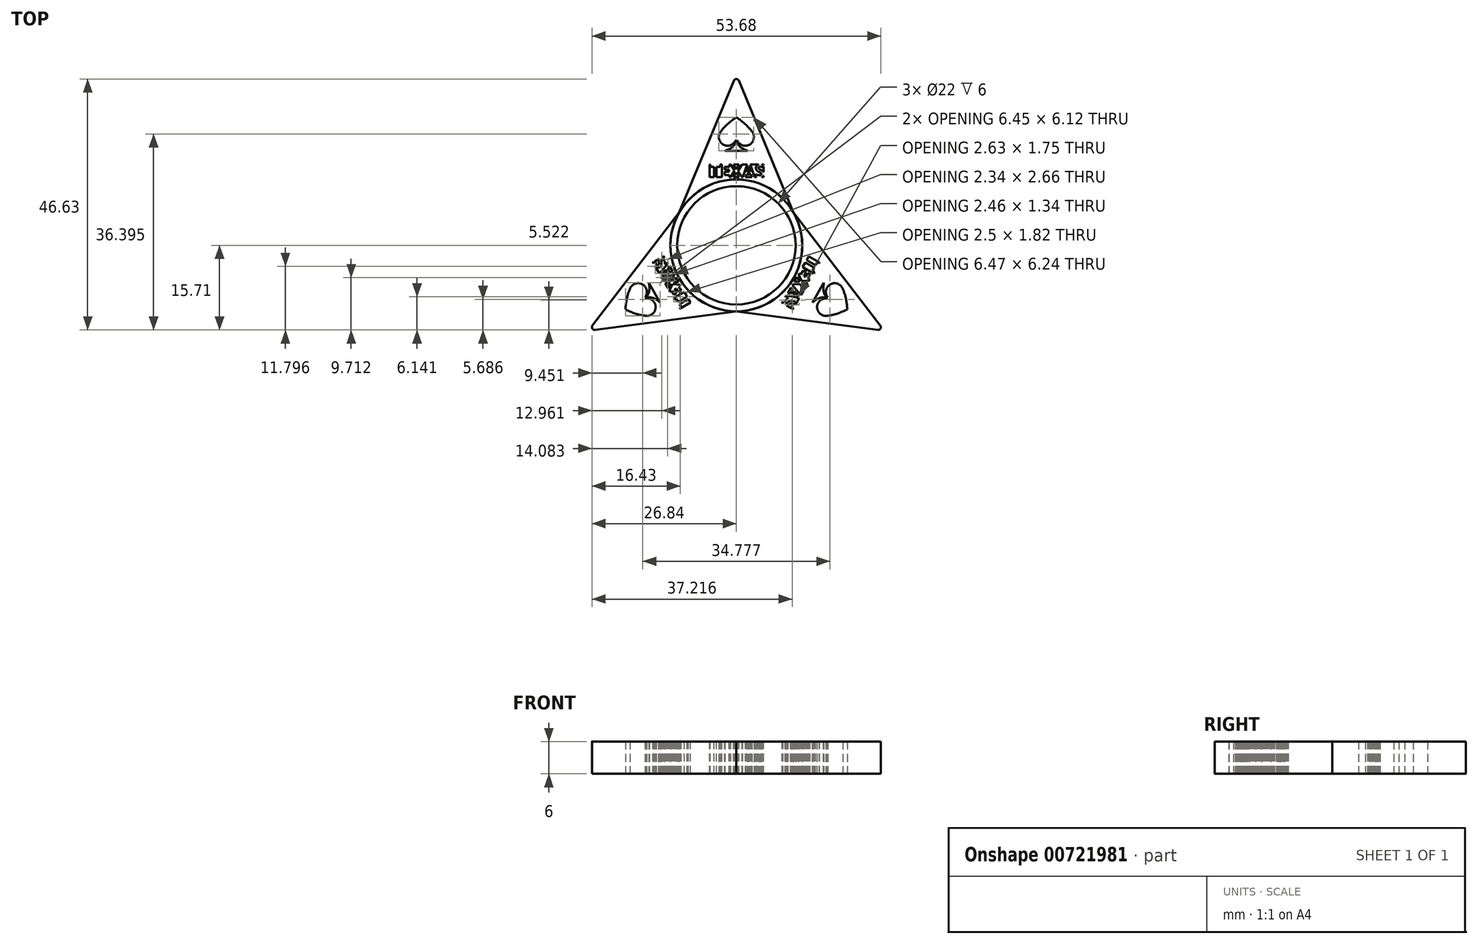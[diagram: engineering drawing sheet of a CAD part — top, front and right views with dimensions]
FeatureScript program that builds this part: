
annotation { "Feature Type Name" : "Feature", "Feature Type Description" : "" }
export const myFeature = defineFeature(function(context is Context, id is Id, definition is map)
    precondition{}
    {
        {
            var Q0;
            Q0=qCreatedBy(makeId("Top.planeOp"),FACE);
            var sketch = newSketch(context, id + "F0", { "sketchPlane" : qUnion([Q0])});
            skCircle(sketch, "E0", {"center": v(0, 0) * mm, "radius": 11 * mm});
            skCircle(sketch, "E1", {"center": v(0, 0) * mm, "radius": 12.25 * mm});
            skLineSegment(sketch, "E2", {"start": v(-10.6, 6.13) * mm, "end": v(-0.47, 30.6) * mm});
            skLineSegment(sketch, "E3", {"start": v(0.47, 30.6) * mm, "end": v(10.6, 6.12) * mm});
            skLineSegment(sketch, "E4", {"start": v(0, 31.74) * mm, "end": v(0, -7.63) * mm, "construction": true});
            skPoint(sketch, "E5", {"position": v(-1.34, 23.8) * mm});
            skArc(sketch, "E6", {"start": v(-2.88, 21.18) * mm, "mid": v(-2.46, 18.73) * mm, "end": v(-0.12, 19.56) * mm});
            skFitSpline(sketch, "E7", {"points": [v(0, 23.8) * mm, v(-0.57, 23.4) * mm, v(-1.6, 22.58) * mm, v(-2.33, 21.86) * mm, v(-2.88, 21.18) * mm], "startDerivative": vector(-2.46, -1.7) * mm, "endDerivative": vector(-2.24, -2.87) * mm});
            skFitSpline(sketch, "E8.MirrorCS", {"points": [v(0, 23.8) * mm, v(0.57, 23.4) * mm, v(1.6, 22.58) * mm, v(2.33, 21.86) * mm, v(2.88, 21.18) * mm], "startDerivative": vector(2.46, -1.7) * mm, "endDerivative": vector(2.24, -2.87) * mm});
            skArc(sketch, "E9.MirrorCS", {"start": v(2.88, 21.18) * mm, "mid": v(2.46, 18.73) * mm, "end": v(0.12, 19.56) * mm});
            skFitSpline(sketch, "E10", {"points": [v(-0.12, 19.56) * mm, v(-0.07, 19.49) * mm, v(-0.12, 19.11) * mm, v(-0.54, 18.48) * mm, v(-0.89, 18.16) * mm, v(-1.38, 17.86) * mm, v(-2.1, 17.56) * mm], "startDerivative": vector(0.67, -0.8) * mm, "endDerivative": vector(-3.48, -1.28) * mm});
            skLineSegment(sketch, "E11", {"start": v(-2.1, 17.56) * mm, "end": v(0, 17.56) * mm});
            skFitSpline(sketch, "E12.MirrorCS", {"points": [v(0.12, 19.56) * mm, v(0.07, 19.49) * mm, v(0.12, 19.11) * mm, v(0.54, 18.48) * mm, v(0.89, 18.16) * mm, v(1.38, 17.86) * mm, v(2.1, 17.56) * mm], "startDerivative": vector(-0.67, -0.8) * mm, "endDerivative": vector(3.48, -1.28) * mm});
            skLineSegment(sketch, "E13.MirrorCS", {"start": v(2.1, 17.56) * mm, "end": v(0, 17.56) * mm});
            skPoint(sketch, "E14.visualSharp", {"position": v(0, 31.74) * mm});
            skArc(sketch, "E14.filletArc", {"start": v(0.47, 30.6) * mm, "mid": v(0, 30.92) * mm, "end": v(-0.47, 30.6) * mm});
            skPoint(sketch, "E15.visualSharp", {"position": v(-27.48, -15.87) * mm});
            skArc(sketch, "E15.filletArc", {"start": v(-26.74, -14.9) * mm, "mid": v(-26.78, -15.46) * mm, "end": v(-26.27, -15.7) * mm});
            skPoint(sketch, "E16.visualSharp", {"position": v(27.48, -15.87) * mm});
            skArc(sketch, "E16.filletArc", {"start": v(26.27, -15.7) * mm, "mid": v(26.78, -15.46) * mm, "end": v(26.74, -14.9) * mm});
            skSolve(sketch);
        }
        {
            var Q0;
            Q0 = qSketchRegion(id + "F0", true);
            extrude(context, id + "F1", {"entities" : qUnion([Q0]), "depth" : 6 * mm, "offsetDistance" : 25.4 * mm});
        }
        {
            var Q0;
            Q0=makeQuery(id+"F1.opExtrude","CAP_FACE",FACE,{"disambiguationData":[OSD([sQuery(id+"F0.wireOp",EDGE,"E0"),sQuery(id+"F0.wireOp",EDGE,"E2"),sQuery(id+"F0.wireOp",EDGE,"E3"),sQuery(id+"F0.wireOp",EDGE,"6553289f-a740-47f3-a68b-70bc11956e42.1.0"),sQuery(id+"F0.wireOp",EDGE,"6553289f-a740-47f3-a68b-70bc11956e42.1.1"),sQuery(id+"F0.wireOp",EDGE,"6553289f-a740-47f3-a68b-70bc11956e42.2.0"),sQuery(id+"F0.wireOp",EDGE,"6553289f-a740-47f3-a68b-70bc11956e42.2.1"),sQuery(id+"F0.wireOp",EDGE,"E6"),sQuery(id+"F0.wireOp",EDGE,"E7"),sQuery(id+"F0.wireOp",EDGE,"E8.MirrorCS"),sQuery(id+"F0.wireOp",EDGE,"E9.MirrorCS"),sQuery(id+"F0.wireOp",EDGE,"E10"),sQuery(id+"F0.wireOp",EDGE,"E11"),sQuery(id+"F0.wireOp",EDGE,"E12.MirrorCS"),sQuery(id+"F0.wireOp",EDGE,"E13.MirrorCS"),sQuery(id+"F0.wireOp",EDGE,"E14.filletArc"),sQuery(id+"F0.wireOp",EDGE,"E15.filletArc"),sQuery(id+"F0.wireOp",EDGE,"E16.filletArc")])],"isStart":false});
            var sketch = newSketch(context, id + "F2", { "sketchPlane" : qUnion([Q0])});
            skText(sketch, "E17", { "text": "TEXAS", "fontName": "OpenSans-Bold.ttf"});
            skPoint(sketch, "E18", {"position": v(0, 15.03) * mm});
            skPoint(sketch, "E19", {"position": v(0.26, 13.84) * mm});
            skPoint(sketch, "E19.positionSnap0", {"position": v(0.2, 13.84) * mm});
            skLineSegment(sketch, "E20", {"start": v(-4.82, 15) * mm, "end": v(-4.82, 12.7) * mm});
            skLineSegment(sketch, "E21", {"start": v(-4.82, 12.7) * mm, "end": v(5.04, 12.7) * mm});
            skLineSegment(sketch, "E22", {"start": v(5.04, 12.7) * mm, "end": v(5.04, 15) * mm});
            skLineSegment(sketch, "E23", {"start": v(5.04, 15) * mm, "end": v(-4.82, 15) * mm});
            skPoint(sketch, "E24", {"position": v(-3.03, 14.9) * mm});
            skPoint(sketch, "E25", {"position": v(-2.66, 14.9) * mm});
            skLineSegment(sketch, "E26", {"start": v(-4.82, 15.11) * mm, "end": v(-5.07, 15.11) * mm});
            const initialGuessF2  = {"E17": [-0.00488, 0.01265, 1, 0, 0.00238]};
            skSetInitialGuess(sketch, initialGuessF2);
            skSolve(sketch);
        }
        {
            var Q0;
            {var subQ1=sQuery(id+"F2.wireOp",EDGE,"E17.sketch_text.stroke-6");Q0=makeQuery(id+"F2.imprint","IMPRINT",FACE,{"disambiguationData":[TD([[makeQuery(id+"F2.imprint","IMPRINT",EDGE,{"derivedFrom":subQ1}),1.0]])]});}
            var Q1;
            {var subQ8=sQuery(id+"F2.wireOp",EDGE,"E17.sketch_text.stroke-12");Q1=makeQuery(id+"F2.imprint","IMPRINT",FACE,{"disambiguationData":[TD([[makeQuery(id+"F2.imprint","IMPRINT",EDGE,{"derivedFrom":subQ8}),1.0]])]});}
            var Q2;
            {var subQ0=sQuery(id+"F2.wireOp",EDGE,"E17.sketch_text.stroke-28");var subQ1=sQuery(id+"F2.wireOp",EDGE,"E17.sketch_text.stroke-27");var subQ2=makeQuery(id+"F2.imprint","INTERSECT",VERTEX,{"derivedFrom":[subQ1,subQ0]});Q2=makeQuery(id+"F2.imprint","IMPRINT",FACE,{"disambiguationData":[TD([[makeQuery(id+"F2.imprint","IMPRINT",EDGE,{"disambiguationData":[TD([[subQ2,1.0]])],"derivedFrom":subQ1}),1.0]])]});}
            var Q3;
            {var subQ0=sQuery(id+"F2.wireOp",EDGE,"E17.sketch_text.stroke-22");var subQ1=sQuery(id+"F2.wireOp",EDGE,"E17.sketch_text.stroke-21");var subQ2=makeQuery(id+"F2.imprint","INTERSECT",VERTEX,{"derivedFrom":[subQ1,subQ0]});Q3=makeQuery(id+"F2.imprint","IMPRINT",FACE,{"disambiguationData":[TD([[makeQuery(id+"F2.imprint","IMPRINT",EDGE,{"disambiguationData":[TD([[subQ2,1.0]])],"derivedFrom":subQ1}),1.0]])]});}
            var Q4;
            {var subQ1=sQuery(id+"F2.wireOp",EDGE,"E17.sketch_text.stroke-31");var subQ5=sQuery(id+"F2.wireOp",EDGE,"E17.sketch_text.stroke-30");var subQ6=makeQuery(id+"F2.imprint","INTERSECT",VERTEX,{"derivedFrom":[subQ5,subQ1]});Q4=makeQuery(id+"F2.imprint","IMPRINT",FACE,{"disambiguationData":[TD([[makeQuery(id+"F2.imprint","IMPRINT",EDGE,{"disambiguationData":[TD([[subQ6,1.0]])],"derivedFrom":subQ5}),1.0]])]});}
            var Q5;
            Q5=makeQuery(id+"F2.imprint","IMPRINT",FACE,{"disambiguationData":[TD([[makeQuery(id+"F2.imprint","IMPRINT",EDGE,{"derivedFrom":sQuery(id+"F2.wireOp",EDGE,"E17.sketch_text.stroke-40")}),1.0]])]});
            var Q6;
            {var subQ0=sQuery(id+"F2.wireOp",EDGE,"E17.sketch_text.stroke-33");Q6=makeQuery(id+"F2.imprint","IMPRINT",FACE,{"disambiguationData":[TD([[makeQuery(id+"F2.imprint","IMPRINT",EDGE,{"derivedFrom":subQ0}),1.0]])]});}
            var Q7;
            {var subQ7=sQuery(id+"F2.wireOp",EDGE,"E17.sketch_text.stroke-47");Q7=makeQuery(id+"F2.imprint","IMPRINT",FACE,{"disambiguationData":[TD([[makeQuery(id+"F2.imprint","IMPRINT",EDGE,{"derivedFrom":subQ7}),1.0]])]});}
            var Q8;
            {var subQ6=sQuery(id+"F2.wireOp",EDGE,"E17.sketch_text.stroke-63");Q8=makeQuery(id+"F2.imprint","IMPRINT",FACE,{"disambiguationData":[TD([[makeQuery(id+"F2.imprint","IMPRINT",EDGE,{"derivedFrom":subQ6}),1.0]])]});}
            var Q9;
            {var subQ0=sQuery(id+"F2.wireOp",EDGE,"E17.sketch_text.stroke-45");var subQ1=sQuery(id+"F2.wireOp",EDGE,"E17.sketch_text.stroke-44");var subQ2=makeQuery(id+"F2.imprint","INTERSECT",VERTEX,{"derivedFrom":[subQ1,subQ0]});Q9=makeQuery(id+"F2.imprint","IMPRINT",FACE,{"disambiguationData":[TD([[makeQuery(id+"F2.imprint","IMPRINT",EDGE,{"disambiguationData":[TD([[subQ2,1.0]])],"derivedFrom":subQ1}),1.0]])]});}
            var Q10;
            {var subQ0=sQuery(id+"F2.wireOp",EDGE,"E17.sketch_text.stroke-61");var subQ1=sQuery(id+"F2.wireOp",EDGE,"E17.sketch_text.stroke-60");var subQ2=makeQuery(id+"F2.imprint","INTERSECT",VERTEX,{"derivedFrom":[subQ1,subQ0]});Q10=makeQuery(id+"F2.imprint","IMPRINT",FACE,{"disambiguationData":[TD([[makeQuery(id+"F2.imprint","IMPRINT",EDGE,{"disambiguationData":[TD([[subQ2,1.0]])],"derivedFrom":subQ1}),1.0]])]});}
            var Q11;
            {var subQ1=sQuery(id+"F2.wireOp",EDGE,"E17.sketch_text.stroke-2");Q11=makeQuery(id+"F2.imprint","IMPRINT",FACE,{"disambiguationData":[TD([[makeQuery(id+"F2.imprint","IMPRINT",EDGE,{"derivedFrom":subQ1}),1.0]])]});}
            extrude(context, id + "F3", {"entities" : qUnion([Q0, Q1, Q2, Q3, Q4, Q5, Q6, Q7, Q8, Q9, Q10, Q11]), "operationType" : NewBodyOperationType.REMOVE, "endBound" : BoundingType.THROUGH_ALL, "oppositeDirection" : true, "depth" : 5.08 * mm, "offsetDistance" : 25.4 * mm});
        }
        {
            var Q0;
            Q0=makeQuery(id+"F1.opExtrude","CAP_FACE",FACE,{"disambiguationData":[OSD([sQuery(id+"F0.wireOp",EDGE,"E0"),sQuery(id+"F0.wireOp",EDGE,"E2"),sQuery(id+"F0.wireOp",EDGE,"E3"),sQuery(id+"F0.wireOp",EDGE,"6553289f-a740-47f3-a68b-70bc11956e42.1.0"),sQuery(id+"F0.wireOp",EDGE,"6553289f-a740-47f3-a68b-70bc11956e42.1.1"),sQuery(id+"F0.wireOp",EDGE,"6553289f-a740-47f3-a68b-70bc11956e42.2.0"),sQuery(id+"F0.wireOp",EDGE,"6553289f-a740-47f3-a68b-70bc11956e42.2.1"),sQuery(id+"F0.wireOp",EDGE,"E6"),sQuery(id+"F0.wireOp",EDGE,"E7"),sQuery(id+"F0.wireOp",EDGE,"E8.MirrorCS"),sQuery(id+"F0.wireOp",EDGE,"E9.MirrorCS"),sQuery(id+"F0.wireOp",EDGE,"E10"),sQuery(id+"F0.wireOp",EDGE,"E11"),sQuery(id+"F0.wireOp",EDGE,"E12.MirrorCS"),sQuery(id+"F0.wireOp",EDGE,"E13.MirrorCS"),sQuery(id+"F0.wireOp",EDGE,"E14.filletArc"),sQuery(id+"F0.wireOp",EDGE,"E15.filletArc"),sQuery(id+"F0.wireOp",EDGE,"E16.filletArc")])],"isStart":false});
            var sketch = newSketch(context, id + "F4", { "sketchPlane" : qUnion([Q0])});
            skLineSegment(sketch, "E27", {"start": v(-4.82, 15) * mm, "end": v(-4.95, 15) * mm});
            skLineSegment(sketch, "E28", {"start": v(-4.95, 15) * mm, "end": v(-4.95, 12.7) * mm});
            skLineSegment(sketch, "E29", {"start": v(-4.95, 12.7) * mm, "end": v(-4.82, 12.7) * mm});
            skLineSegment(sketch, "E30", {"start": v(-4.82, 12.7) * mm, "end": v(-4.82, 15) * mm});
            skSolve(sketch);
        }
        {
            var Q0;
            Q0 = qSketchRegion(id + "F4", true);
            extrude(context, id + "F5", {"entities" : qUnion([Q0]), "operationType" : NewBodyOperationType.REMOVE, "endBound" : BoundingType.THROUGH_ALL, "oppositeDirection" : true, "depth" : 25.4 * mm, "offsetDistance" : 25.4 * mm});
        }
        {
            var Q0;
            Q0=makeQuery(id+"F1.opExtrude","SWEPT_BODY",BODY,{"disambiguationData":[OSD([sQuery(id+"F0.wireOp",EDGE,"E0"),sQuery(id+"F0.wireOp",EDGE,"E1"),sQuery(id+"F0.wireOp",EDGE,"E2"),sQuery(id+"F0.wireOp",EDGE,"E3"),sQuery(id+"F0.wireOp",EDGE,"E6"),sQuery(id+"F0.wireOp",EDGE,"E7"),sQuery(id+"F0.wireOp",EDGE,"E8.MirrorCS"),sQuery(id+"F0.wireOp",EDGE,"E9.MirrorCS"),sQuery(id+"F0.wireOp",EDGE,"E10"),sQuery(id+"F0.wireOp",EDGE,"E11"),sQuery(id+"F0.wireOp",EDGE,"E12.MirrorCS"),sQuery(id+"F0.wireOp",EDGE,"E13.MirrorCS"),sQuery(id+"F0.wireOp",EDGE,"E14.filletArc")])]});
            var Q1;
            Q1=makeQuery(id+"F1.opExtrude","CAP_EDGE",EDGE,{"disambiguationData":[OSD([sQuery(id+"F0.wireOp",EDGE,"E0")])],"isStart":false});
            circularPattern(context, id + "F6", {"entities" : qUnion([Q0]), "axis" : qUnion([Q1]), "angle" : 360 * degree, "instanceCount" : 3, "equalSpace" : true});
        }
    });
